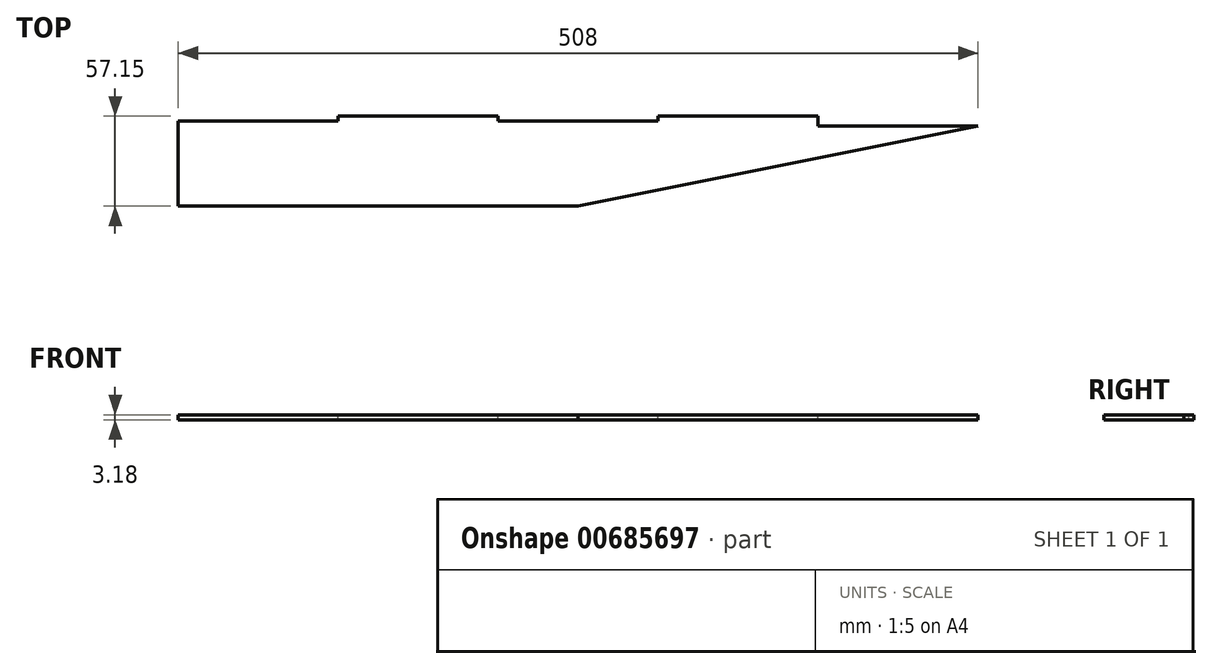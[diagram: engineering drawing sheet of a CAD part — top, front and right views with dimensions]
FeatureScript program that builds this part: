
annotation { "Feature Type Name" : "Feature", "Feature Type Description" : "" }
export const myFeature = defineFeature(function(context is Context, id is Id, definition is map)
    precondition{}
    {
        {
            var Q0;
            Q0=qCreatedBy(makeId("Top.planeOp"),FACE);
            var sketch = newSketch(context, id + "F0", { "sketchPlane" : qUnion([Q0])});
            skLineSegment(sketch, "E0.bottom", {"start": v(0, 0) * mm, "end": v(508, 0) * mm});
            skLineSegment(sketch, "E0.top", {"start": v(0, 57.15) * mm, "end": v(508, 57.15) * mm});
            skLineSegment(sketch, "E0.left", {"start": v(0, 0) * mm, "end": v(0, 57.15) * mm});
            skLineSegment(sketch, "E0.right", {"start": v(508, 0) * mm, "end": v(508, 57.15) * mm});
            skSolve(sketch);
        }
        {
            var Q0;
            Q0 = qSketchRegion(id + "F0", true);
            var Q1;
            Q1=makeQuery(id+"F0.imprint","IMPRINT",FACE,{"disambiguationData":[TD([[makeQuery(id+"F0.imprint","IMPRINT",EDGE,{"derivedFrom":sQuery(id+"F0.wireOp",EDGE,"E0.bottom")}),1.0]])]});
            extrude(context, id + "F1", {"entities" : qUnion([Q0, Q1]), "depth" : 3.17 * mm, "offsetDistance" : 25.4 * mm});
        }
        {
            var Q0;
            Q0=makeQuery(id+"F1.opExtrude","CAP_FACE",FACE,{"disambiguationData":[OSD([sQuery(id+"F0.wireOp",EDGE,"E0.bottom"),sQuery(id+"F0.wireOp",EDGE,"E0.top"),sQuery(id+"F0.wireOp",EDGE,"E0.left"),sQuery(id+"F0.wireOp",EDGE,"E0.right")])],"isStart":false});
            var sketch = newSketch(context, id + "F2", { "sketchPlane" : qUnion([Q0])});
            skLineSegment(sketch, "E1.left", {"start": v(101.6, 57.15) * mm, "end": v(101.6, 53.98) * mm});
            skLineSegment(sketch, "E1.right", {"start": v(203.2, 57.15) * mm, "end": v(203.2, 53.98) * mm});
            skLineSegment(sketch, "E2.left", {"start": v(304.8, 57.15) * mm, "end": v(304.8, 53.98) * mm});
            skLineSegment(sketch, "E2.right", {"start": v(406.4, 57.15) * mm, "end": v(406.4, 53.98) * mm});
            skLineSegment(sketch, "E3.bottom", {"start": v(101.6, 53.98) * mm, "end": v(0, 53.98) * mm});
            skLineSegment(sketch, "E3.top", {"start": v(101.6, 57.15) * mm, "end": v(0, 57.15) * mm});
            skLineSegment(sketch, "E3.left", {"start": v(101.6, 53.98) * mm, "end": v(101.6, 57.15) * mm});
            skLineSegment(sketch, "E3.right", {"start": v(0, 53.98) * mm, "end": v(0, 57.15) * mm});
            skLineSegment(sketch, "E4.bottom", {"start": v(203.2, 53.98) * mm, "end": v(304.8, 53.98) * mm});
            skLineSegment(sketch, "E4.top", {"start": v(203.2, 57.15) * mm, "end": v(304.8, 57.15) * mm});
            skLineSegment(sketch, "E4.left", {"start": v(203.2, 53.98) * mm, "end": v(203.2, 57.15) * mm});
            skLineSegment(sketch, "E4.right", {"start": v(304.8, 53.98) * mm, "end": v(304.8, 57.15) * mm});
            skLineSegment(sketch, "E5.bottom", {"start": v(406.4, 53.98) * mm, "end": v(508, 53.98) * mm});
            skLineSegment(sketch, "E5.top", {"start": v(406.4, 57.15) * mm, "end": v(508, 57.15) * mm});
            skLineSegment(sketch, "E5.left", {"start": v(406.4, 53.98) * mm, "end": v(406.4, 57.15) * mm});
            skLineSegment(sketch, "E5.right", {"start": v(508, 53.98) * mm, "end": v(508, 57.15) * mm});
            skSolve(sketch);
        }
        {
            var Q0;
            Q0=makeQuery(id+"F1.opExtrude","CAP_FACE",FACE,{"disambiguationData":[OSD([sQuery(id+"F0.wireOp",EDGE,"E0.bottom"),sQuery(id+"F0.wireOp",EDGE,"E0.top"),sQuery(id+"F0.wireOp",EDGE,"E0.left"),sQuery(id+"F0.wireOp",EDGE,"E0.right")])],"isStart":false});
            var sketch = newSketch(context, id + "F3", { "sketchPlane" : qUnion([Q0])});
            skLineSegment(sketch, "E6", {"start": v(254, 0) * mm, "end": v(508, 50.8) * mm});
            skLineSegment(sketch, "E7", {"start": v(254, 0) * mm, "end": v(508, 0) * mm});
            skLineSegment(sketch, "E8", {"start": v(508, 0) * mm, "end": v(508, 57.15) * mm});
            skSolve(sketch);
        }
        {
            var Q0;
            {var subQ0=sQuery(id+"F3.wireOp",EDGE,"E6");Q0=makeQuery(id+"F3.imprint","IMPRINT",FACE,{"disambiguationData":[TD([[makeQuery(id+"F3.imprint","IMPRINT",EDGE,{"derivedFrom":subQ0}),-1.0]])]});}
            extrude(context, id + "F4", {"entities" : qUnion([Q0]), "operationType" : NewBodyOperationType.REMOVE, "oppositeDirection" : true, "depth" : 25.4 * mm, "offsetDistance" : 25.4 * mm});
        }
        {
            var Q0;
            Q0 = qSketchRegion(id + "F2", true);
            extrude(context, id + "F5", {"entities" : qUnion([Q0]), "operationType" : NewBodyOperationType.REMOVE, "oppositeDirection" : true, "depth" : 25.4 * mm, "offsetDistance" : 25.4 * mm});
        }
        {
            var Q0;
            Q0=makeQuery(id+"F1.opExtrude","CAP_FACE",FACE,{"disambiguationData":[OSD([sQuery(id+"F0.wireOp",EDGE,"E0.bottom"),sQuery(id+"F0.wireOp",EDGE,"E0.top"),sQuery(id+"F0.wireOp",EDGE,"E0.left"),sQuery(id+"F0.wireOp",EDGE,"E0.right")])],"isStart":false});
            var sketch = newSketch(context, id + "F6", { "sketchPlane" : qUnion([Q0])});
            skLineSegment(sketch, "E9.bottom", {"start": v(508, 50.8) * mm, "end": v(406.4, 50.8) * mm});
            skLineSegment(sketch, "E9.top", {"start": v(508, 53.98) * mm, "end": v(406.4, 53.98) * mm});
            skLineSegment(sketch, "E9.left", {"start": v(508, 50.8) * mm, "end": v(508, 53.98) * mm});
            skLineSegment(sketch, "E9.right", {"start": v(406.4, 50.8) * mm, "end": v(406.4, 53.98) * mm});
            skSolve(sketch);
        }
        {
            var Q0;
            Q0 = qSketchRegion(id + "F6", true);
            extrude(context, id + "F7", {"entities" : qUnion([Q0]), "operationType" : NewBodyOperationType.REMOVE, "oppositeDirection" : true, "depth" : 25.4 * mm, "offsetDistance" : 25.4 * mm});
        }
    });
